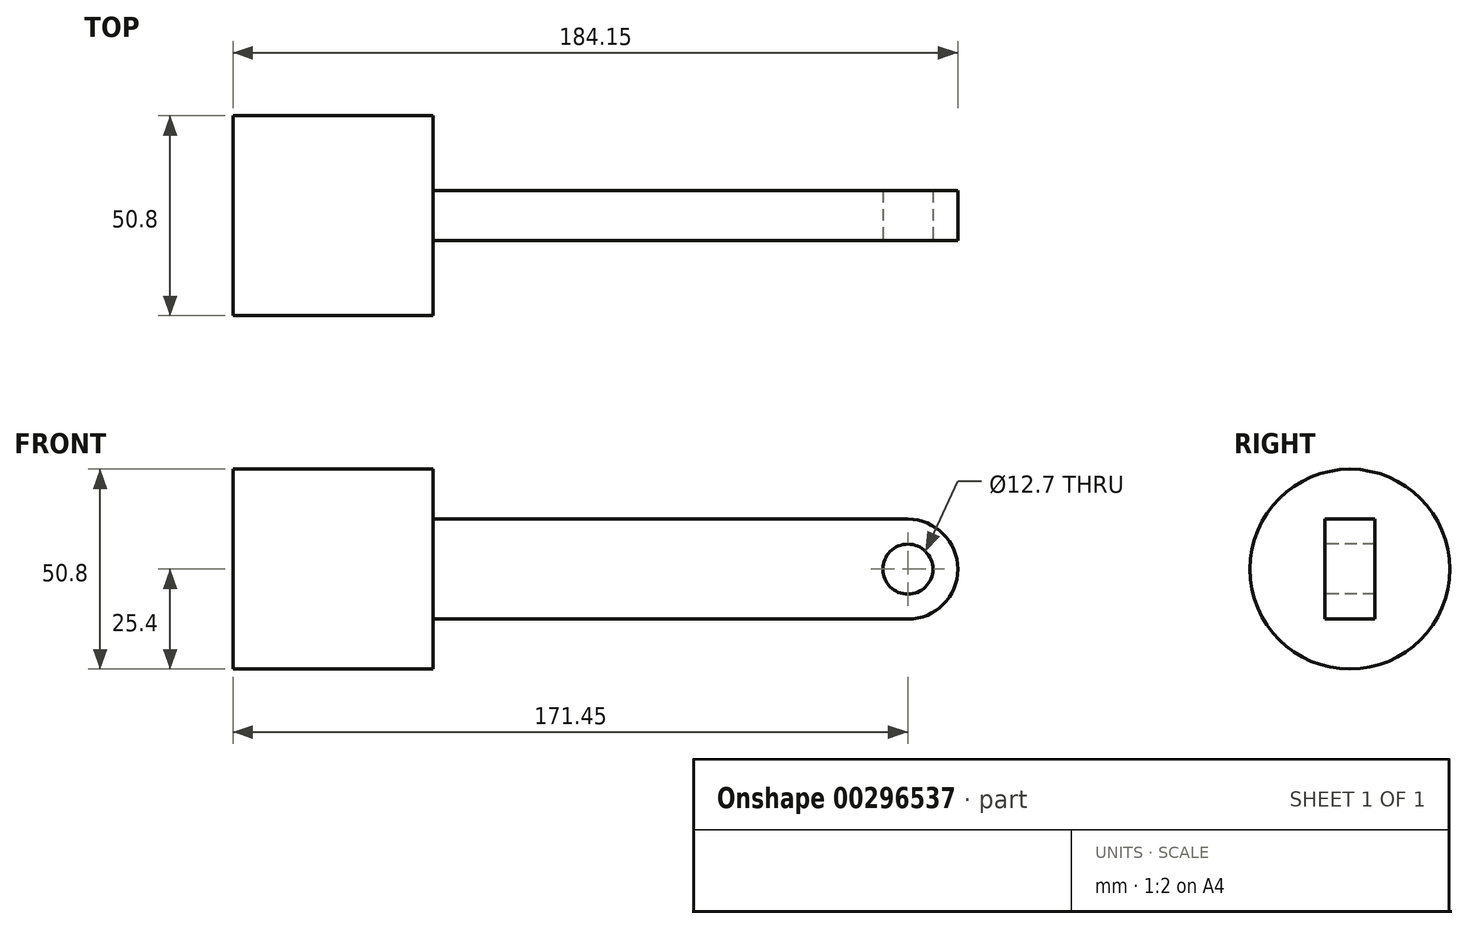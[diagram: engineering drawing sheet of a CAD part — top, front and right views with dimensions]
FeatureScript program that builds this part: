
annotation { "Feature Type Name" : "Feature", "Feature Type Description" : "" }
export const myFeature = defineFeature(function(context is Context, id is Id, definition is map)
    precondition{}
    {
        {
            var Q0;
            Q0=qCreatedBy(makeId("Right.planeOp"),FACE);
            var sketch = newSketch(context, id + "F0", { "sketchPlane" : qUnion([Q0])});
            skCircle(sketch, "E0", {"center": v(0, 0) * mm, "radius": 25.4 * mm});
            skSolve(sketch);
        }
        {
            var Q0;
            Q0=makeQuery(id+"F0.imprint","IMPRINT",FACE,{"disambiguationData":[TD([[makeQuery(id+"F0.imprint","IMPRINT",EDGE,{"derivedFrom":sQuery(id+"F0.wireOp",EDGE,"E0")}),1.0]])]});
            extrude(context, id + "F1", {"entities" : qUnion([Q0]), "oppositeDirection" : true, "depth" : 50.8 * mm});
        }
        {
            var Q0;
            Q0=makeQuery(id+"F1.opExtrude","CAP_FACE",FACE,{"disambiguationData":[OSD([sQuery(id+"F0.wireOp",EDGE,"E0")])],"isStart":true});
            var sketch = newSketch(context, id + "F2", { "sketchPlane" : qUnion([Q0])});
            skLineSegment(sketch, "E1.bottom", {"start": v(-6.35, 12.7) * mm, "end": v(6.35, 12.7) * mm});
            skLineSegment(sketch, "E1.top", {"start": v(-6.35, -12.7) * mm, "end": v(6.35, -12.7) * mm});
            skLineSegment(sketch, "E1.left", {"start": v(-6.35, 12.7) * mm, "end": v(-6.35, -12.7) * mm});
            skLineSegment(sketch, "E1.right", {"start": v(6.35, 12.7) * mm, "end": v(6.35, -12.7) * mm});
            skSolve(sketch);
        }
        {
            var Q0;
            Q0=makeQuery(id+"F2.imprint","IMPRINT",FACE,{"disambiguationData":[TD([[makeQuery(id+"F2.imprint","IMPRINT",EDGE,{"derivedFrom":sQuery(id+"F2.wireOp",EDGE,"E1.bottom")}),-1.0]])]});
            extrude(context, id + "F3", {"entities" : qUnion([Q0]), "operationType" : NewBodyOperationType.ADD, "depth" : 133.35 * mm});
        }
        {
            var Q0;
            Q0=makeQuery(id+"F3.opExtrude","CAP_EDGE",EDGE,{"disambiguationData":[OSD([sQuery(id+"F2.wireOp",EDGE,"E1.bottom")])],"isStart":false});
            var Q1;
            Q1=makeQuery(id+"F3.opExtrude","CAP_EDGE",EDGE,{"disambiguationData":[OSD([sQuery(id+"F2.wireOp",EDGE,"E1.top")])],"isStart":false});
            fillet(context, id + "F4", {"entities" : qUnion([Q0, Q1]), "radius" : 12.7 * mm, "tangentPropagation" : true, "allowEdgeOverflow" : false});
        }
        {
            var Q0;
            Q0=makeQuery(id+"F3.opExtrude","SWEPT_FACE",FACE,{"disambiguationData":[OSD([sQuery(id+"F2.wireOp",EDGE,"E1.left")])]});
            var sketch = newSketch(context, id + "F5", { "sketchPlane" : qUnion([Q0])});
            skCircle(sketch, "E2", {"center": v(120.65, 0) * mm, "radius": 6.35 * mm});
            skSolve(sketch);
        }
        {
            var Q0;
            Q0=makeQuery(id+"F5.imprint","IMPRINT",FACE,{"disambiguationData":[TD([[makeQuery(id+"F5.imprint","IMPRINT",EDGE,{"derivedFrom":sQuery(id+"F5.wireOp",EDGE,"E2")}),1.0]])]});
            extrude(context, id + "F6", {"entities" : qUnion([Q0]), "operationType" : NewBodyOperationType.REMOVE, "endBound" : BoundingType.THROUGH_ALL, "oppositeDirection" : true, "depth" : 25.4 * mm});
        }
    });
